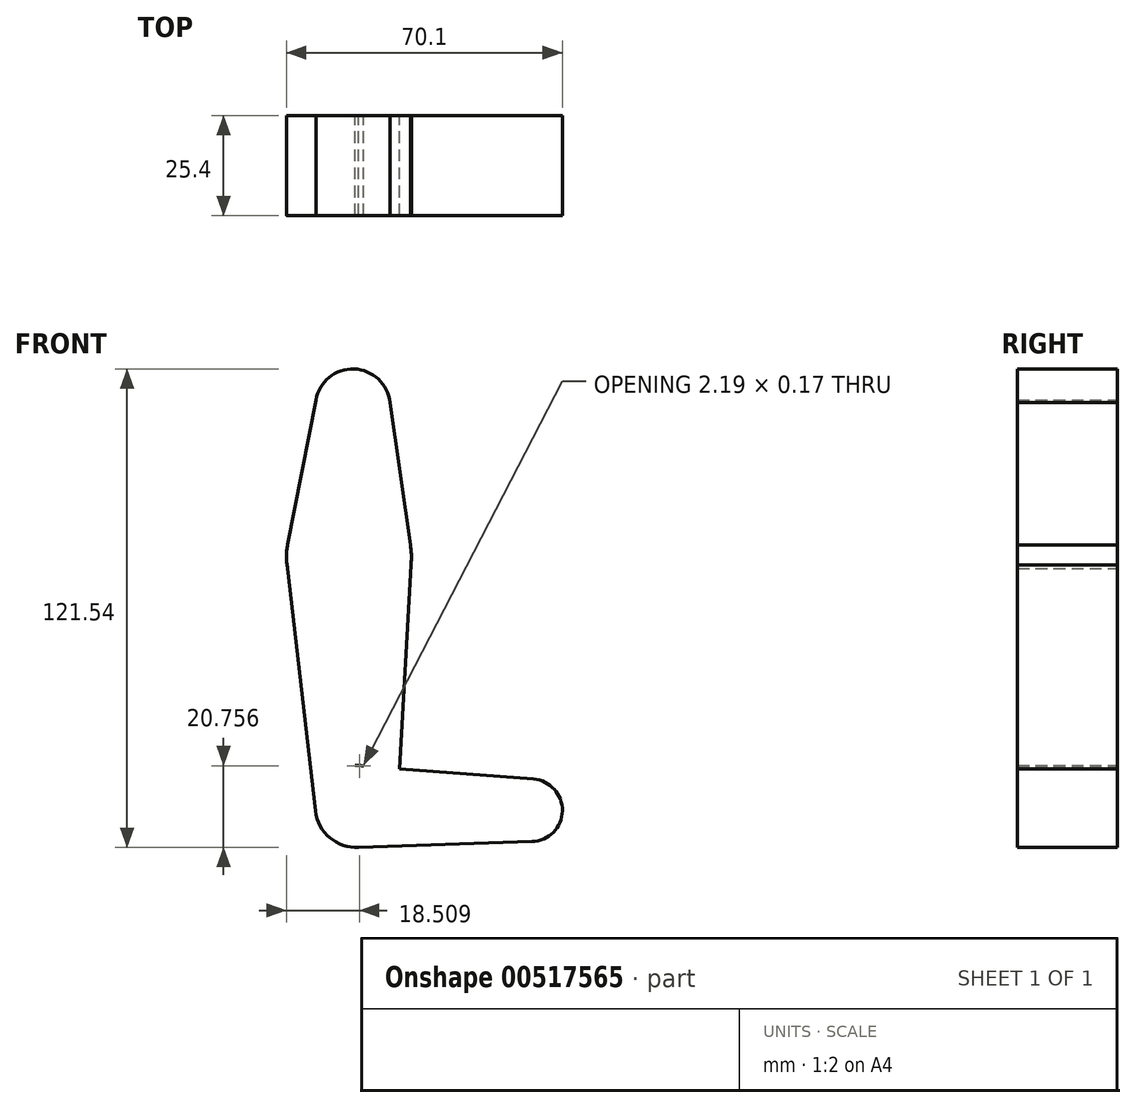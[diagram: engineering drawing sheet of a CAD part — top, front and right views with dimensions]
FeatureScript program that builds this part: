
annotation { "Feature Type Name" : "Feature", "Feature Type Description" : "" }
export const myFeature = defineFeature(function(context is Context, id is Id, definition is map)
    precondition{}
    {
        {
            var Q0;
            Q0=qCreatedBy(makeId("Front.planeOp"),FACE);
            var sketch = newSketch(context, id + "F0", { "sketchPlane" : qUnion([Q0])});
            skCircle(sketch, "E0", {"center": v(-15.88, 78.6) * mm, "radius": 9.53 * mm});
            skCircle(sketch, "E1", {"center": v(-16.88, 40.48) * mm, "radius": 15.88 * mm});
            skCircle(sketch, "E2", {"center": v(-15.04, -23) * mm, "radius": 10.42 * mm});
            skLineSegment(sketch, "E3", {"start": v(-15.88, 78.6) * mm, "end": v(-16.88, 40.48) * mm, "construction": true});
            skLineSegment(sketch, "E4", {"start": v(-15.04, -23) * mm, "end": v(-16.88, 40.48) * mm, "construction": true});
            skCircle(sketch, "E5", {"center": v(29.41, -23.98) * mm, "radius": 7.94 * mm});
            skLineSegment(sketch, "E6", {"start": v(-15.04, -23) * mm, "end": v(29.41, -23.98) * mm, "construction": true});
            skLineSegment(sketch, "E7", {"start": v(-6.41, 79.62) * mm, "end": v(-1.08, 42.04) * mm});
            skLineSegment(sketch, "E8", {"start": v(-1.16, 38.28) * mm, "end": v(-4.6, -23.22) * mm});
            skLineSegment(sketch, "E9", {"start": v(-15.34, -12.57) * mm, "end": v(30.02, -16.06) * mm});
            skLineSegment(sketch, "E10", {"start": v(-14.98, -33.41) * mm, "end": v(29.68, -31.9) * mm});
            skLineSegment(sketch, "E11", {"start": v(-25.27, 80.21) * mm, "end": v(-32.46, 43.53) * mm});
            skLineSegment(sketch, "E12", {"start": v(-32.46, 43.53) * mm, "end": v(-32.46, 37.43) * mm});
            skLineSegment(sketch, "E13", {"start": v(-32.46, 37.43) * mm, "end": v(-25.4, -24.18) * mm});
            skSolve(sketch);
        }
        {
            var Q0;
            Q0 = qSketchRegion(id + "F0", true);
            extrude(context, id + "F1", {"entities" : qUnion([Q0]), "depth" : 25.4 * mm, "offsetDistance" : 25.4 * mm});
        }
    });
